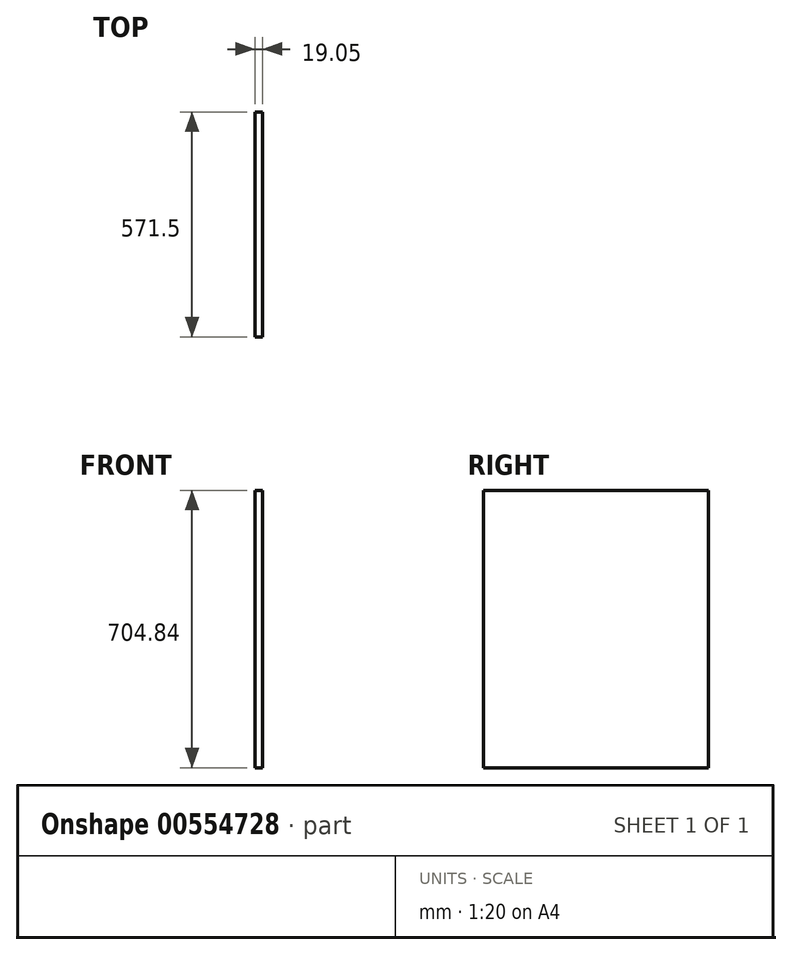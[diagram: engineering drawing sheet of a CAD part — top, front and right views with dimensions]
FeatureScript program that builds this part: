
annotation { "Feature Type Name" : "Feature", "Feature Type Description" : "" }
export const myFeature = defineFeature(function(context is Context, id is Id, definition is map)
    precondition{}
    {
        {
            var Q0;
            Q0=qCreatedBy(makeId("Right.planeOp"),FACE);
            var sketch = newSketch(context, id + "F0", { "sketchPlane" : qUnion([Q0])});
            skLineSegment(sketch, "E0.bottom", {"start": v(285.75, 517.52) * mm, "end": v(-285.75, 517.52) * mm});
            skLineSegment(sketch, "E0.top", {"start": v(285.75, -517.52) * mm, "end": v(-285.75, -517.52) * mm});
            skLineSegment(sketch, "E0.left", {"start": v(285.75, 517.52) * mm, "end": v(285.75, -517.52) * mm});
            skLineSegment(sketch, "E0.right", {"start": v(-285.75, 517.52) * mm, "end": v(-285.75, -517.52) * mm});
            skPoint(sketch, "E0.middle", {"position": v(0, 0) * mm});
            skSolve(sketch);
        }
        {
            var Q0;
            Q0=makeQuery(id+"F0.imprint","IMPRINT",FACE,{"disambiguationData":[TD([[makeQuery(id+"F0.imprint","IMPRINT",EDGE,{"derivedFrom":sQuery(id+"F0.wireOp",EDGE,"E0.bottom")}),1.0]])]});
            extrude(context, id + "F1", {"entities" : qUnion([Q0]), "depth" : 19.05 * mm, "offsetDistance" : 25.4 * mm});
        }
        {
            var Q0;
            Q0=makeQuery(id+"F1.opExtrude","SWEPT_FACE",FACE,{"disambiguationData":[OSD([sQuery(id+"F0.wireOp",EDGE,"E0.bottom")])]});
            extrude(context, id + "F2", {"entities" : qUnion([Q0]), "operationType" : NewBodyOperationType.REMOVE, "oppositeDirection" : true, "depth" : 330.2 * mm, "offsetDistance" : 25.4 * mm});
        }
    });
